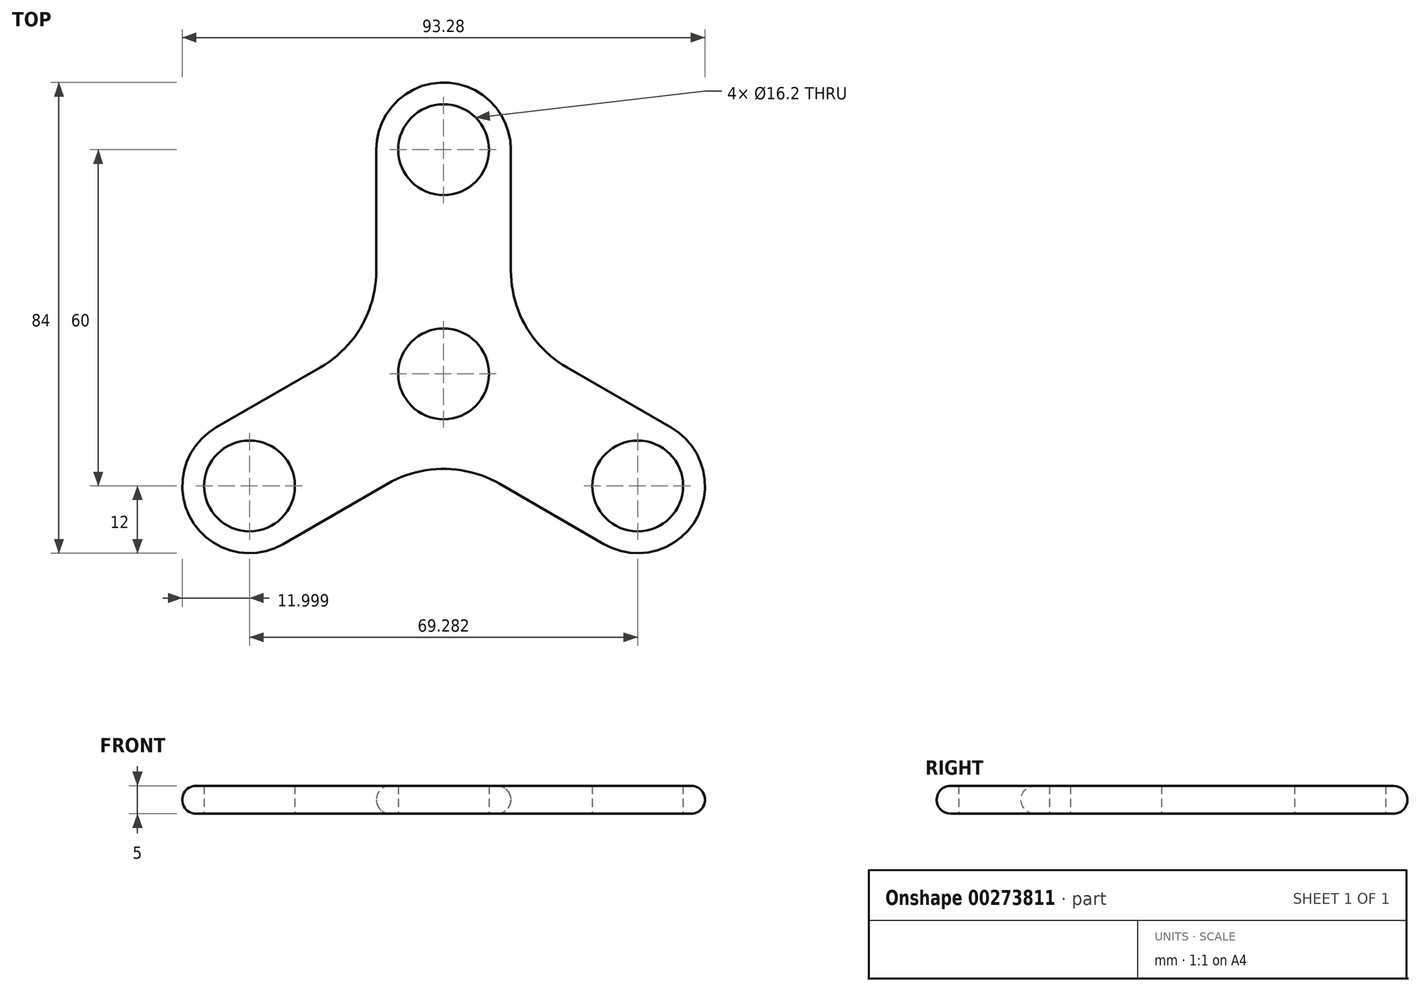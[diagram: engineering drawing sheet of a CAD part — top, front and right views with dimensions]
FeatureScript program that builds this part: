
annotation { "Feature Type Name" : "Feature", "Feature Type Description" : "" }
export const myFeature = defineFeature(function(context is Context, id is Id, definition is map)
    precondition{}
    {
        {
            var Q0;
            Q0=qCreatedBy(makeId("Top.planeOp"),FACE);
            var sketch = newSketch(context, id + "F0", { "sketchPlane" : qUnion([Q0])});
            skCircle(sketch, "E0", {"center": v(0, 0) * mm, "radius": 12 * mm, "construction": true});
            skArc(sketch, "E1", {"start": v(12, 40) * mm, "mid": v(0, 52) * mm, "end": v(-12, 40) * mm});
            skArc(sketch, "E2.1.0", {"start": v(28.64, -30.4) * mm, "mid": v(45.03, -26) * mm, "end": v(40.64, -9.6) * mm});
            skArc(sketch, "E2.2.0", {"start": v(-40.64, -9.6) * mm, "mid": v(-45.03, -26) * mm, "end": v(-28.64, -30.4) * mm});
            skLineSegment(sketch, "E2.anchor1", {"start": v(0, 0) * mm, "end": v(0, 40) * mm, "construction": true});
            skLineSegment(sketch, "E2.anchor2", {"start": v(0, 0) * mm, "end": v(-34.64, -20) * mm, "construction": true});
            skLineSegment(sketch, "E3", {"start": v(34.64, -20) * mm, "end": v(-56.98, 32.9) * mm, "construction": true});
            skLineSegment(sketch, "E4", {"start": v(-12, 40) * mm, "end": v(-12, 6.93) * mm});
            skLineSegment(sketch, "E5", {"start": v(-12, 6.93) * mm, "end": v(-40.64, -9.6) * mm});
            skLineSegment(sketch, "E6", {"start": v(-28.64, -30.4) * mm, "end": v(0, -13.86) * mm});
            skLineSegment(sketch, "E7", {"start": v(0, -13.86) * mm, "end": v(28.64, -30.4) * mm});
            skLineSegment(sketch, "E8", {"start": v(40.64, -9.6) * mm, "end": v(12, 6.93) * mm});
            skLineSegment(sketch, "E9", {"start": v(12, 6.93) * mm, "end": v(12, 40) * mm});
            skSolve(sketch);
        }
        {
            var Q0;
            Q0=makeQuery(id+"F0.imprint","IMPRINT",FACE,{"disambiguationData":[TD([[makeQuery(id+"F0.imprint","IMPRINT",EDGE,{"derivedFrom":sQuery(id+"F0.wireOp",EDGE,"E1")}),1.0]])]});
            extrude(context, id + "F1", {"entities" : qUnion([Q0]), "depth" : 5 * mm});
        }
        {
            var Q0;
            Q0=sQuery(id+"F0.wireOp",VERTEX,"E1.center");
            var Q1;
            Q1=sQuery(id+"F0.wireOp",VERTEX,"E0.center");
            var Q2;
            Q2=sQuery(id+"F0.wireOp",VERTEX,"E3.start");
            var Q3;
            Q3=sQuery(id+"F0.wireOp",VERTEX,"E2.2.0.center");
            var Q4;
            Q4=makeQuery(id+"F1.opExtrude","SWEPT_BODY",BODY,{"disambiguationData":[OSD([sQuery(id+"F0.wireOp",EDGE,"E1"),sQuery(id+"F0.wireOp",EDGE,"E2.1.0"),sQuery(id+"F0.wireOp",EDGE,"E2.2.0"),sQuery(id+"F0.wireOp",EDGE,"E4"),sQuery(id+"F0.wireOp",EDGE,"E5"),sQuery(id+"F0.wireOp",EDGE,"E6"),sQuery(id+"F0.wireOp",EDGE,"E7"),sQuery(id+"F0.wireOp",EDGE,"E8"),sQuery(id+"F0.wireOp",EDGE,"E9")])]});
            hole(context, id + "F2", {"style" : HoleStyle.SIMPLE, "endStyle" : HoleEndStyle.THROUGH, "oppositeDirection" : true, "holeDiameter" : 16.2 * mm, "tappedDepth" : 12 * mm, "tapClearance" : 3, "locations" : qUnion([Q0, Q1, Q2, Q3]), "scope" : qUnion([Q4])});
        }
        {
            var Q0;
            Q0=makeQuery(id+"F1.opExtrude","SWEPT_EDGE",EDGE,{"disambiguationData":[OSD([sQuery(id+"F0.wireOp",EDGE,"E4"),sQuery(id+"F0.wireOp",EDGE,"E5")])]});
            var Q1;
            Q1=makeQuery(id+"F1.opExtrude","SWEPT_EDGE",EDGE,{"disambiguationData":[OSD([sQuery(id+"F0.wireOp",EDGE,"E6"),sQuery(id+"F0.wireOp",EDGE,"E7")])]});
            var Q2;
            Q2=makeQuery(id+"F1.opExtrude","SWEPT_EDGE",EDGE,{"disambiguationData":[OSD([sQuery(id+"F0.wireOp",EDGE,"E8"),sQuery(id+"F0.wireOp",EDGE,"E9")])]});
            fillet(context, id + "F3", {"entities" : qUnion([Q0, Q1, Q2]), "radius" : 20 * mm, "tangentPropagation" : true, "allowEdgeOverflow" : false});
        }
        {
            var Q0;
            Q0=makeQuery(id+"F1.opExtrude","CAP_EDGE",EDGE,{"disambiguationData":[OSD([sQuery(id+"F0.wireOp",EDGE,"E6")])],"isStart":true});
            var Q1;
            Q1=makeQuery(id+"F1.opExtrude","CAP_EDGE",EDGE,{"disambiguationData":[OSD([sQuery(id+"F0.wireOp",EDGE,"E6")])],"isStart":false});
            fillet(context, id + "F4", {"entities" : qUnion([Q0, Q1]), "radius" : 2.5 * mm, "tangentPropagation" : true, "allowEdgeOverflow" : false});
        }
    });
